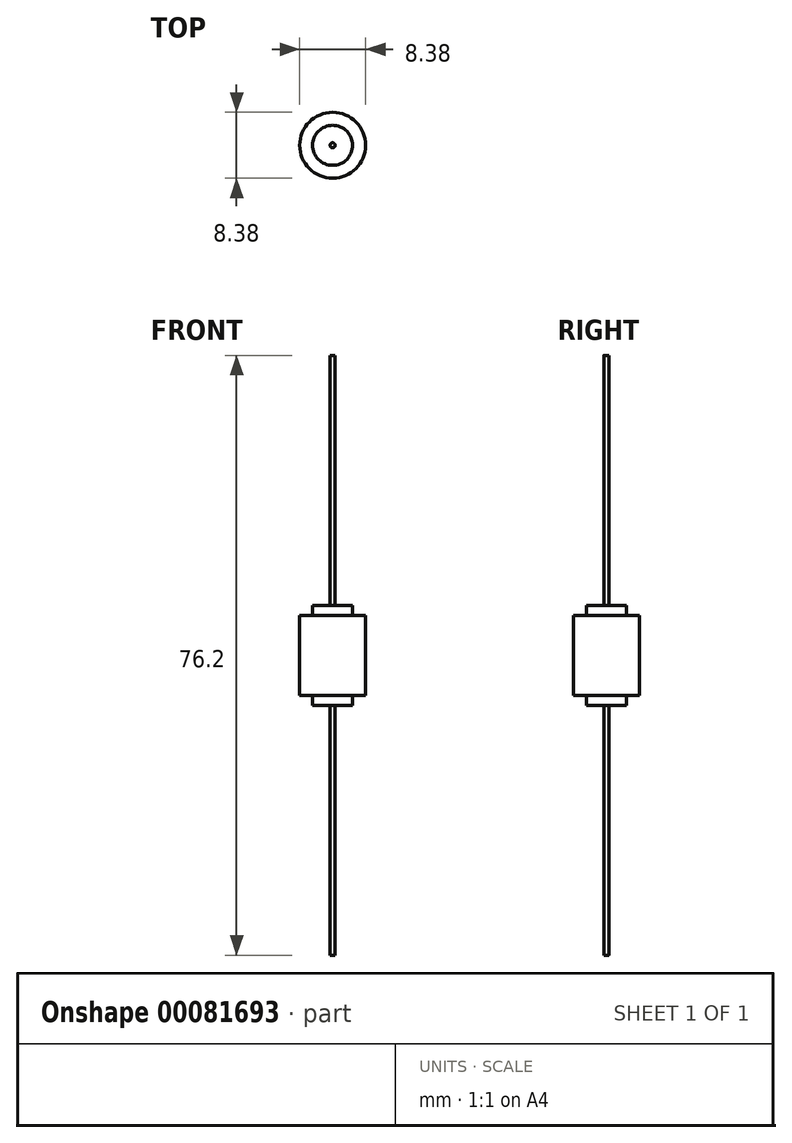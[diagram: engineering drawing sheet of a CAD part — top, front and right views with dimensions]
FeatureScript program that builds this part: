
annotation { "Feature Type Name" : "Feature", "Feature Type Description" : "" }
export const myFeature = defineFeature(function(context is Context, id is Id, definition is map)
    precondition{}
    {
        {
            var Q0;
            Q0=qCreatedBy(makeId("Top.planeOp"),FACE);
            var sketch = newSketch(context, id + "F0", { "sketchPlane" : qUnion([Q0])});
            skCircle(sketch, "E0", {"center": v(0, 0) * mm, "radius": 4.2 * mm});
            skCircle(sketch, "E1", {"center": v(0, 0) * mm, "radius": 2.54 * mm});
            skCircle(sketch, "E2", {"center": v(0, 0) * mm, "radius": 0.32 * mm});
            skSolve(sketch);
        }
        {
            var Q0;
            Q0=makeQuery(id+"F0.imprint","IMPRINT",FACE,{"disambiguationData":[TD([[makeQuery(id+"F0.imprint","IMPRINT",EDGE,{"derivedFrom":sQuery(id+"F0.wireOp",EDGE,"E2")}),1.0]])]});
            extrude(context, id + "F1", {"entities" : qUnion([Q0]), "depth" : 38.1 * mm, "hasSecondDirection" : true, "secondDirectionOppositeDirection" : true, "secondDirectionDepth" : 38.1 * mm});
        }
        {
            var Q0;
            Q0=makeQuery(id+"F0.imprint","IMPRINT",FACE,{"disambiguationData":[TD([[makeQuery(id+"F0.imprint","IMPRINT",EDGE,{"derivedFrom":sQuery(id+"F0.wireOp",EDGE,"E1")}),1.0]])]});
            extrude(context, id + "F2", {"entities" : qUnion([Q0]), "operationType" : NewBodyOperationType.ADD, "depth" : 6.35 * mm, "hasSecondDirection" : true, "secondDirectionOppositeDirection" : true, "secondDirectionDepth" : 6.35 * mm});
        }
        {
            var Q0;
            Q0=makeQuery(id+"F0.imprint","IMPRINT",FACE,{"disambiguationData":[TD([[makeQuery(id+"F0.imprint","IMPRINT",EDGE,{"derivedFrom":sQuery(id+"F0.wireOp",EDGE,"E0")}),1.0]])]});
            extrude(context, id + "F3", {"entities" : qUnion([Q0]), "operationType" : NewBodyOperationType.ADD, "depth" : 5.08 * mm, "hasSecondDirection" : true, "secondDirectionOppositeDirection" : true, "secondDirectionDepth" : 5.08 * mm});
        }
    });
